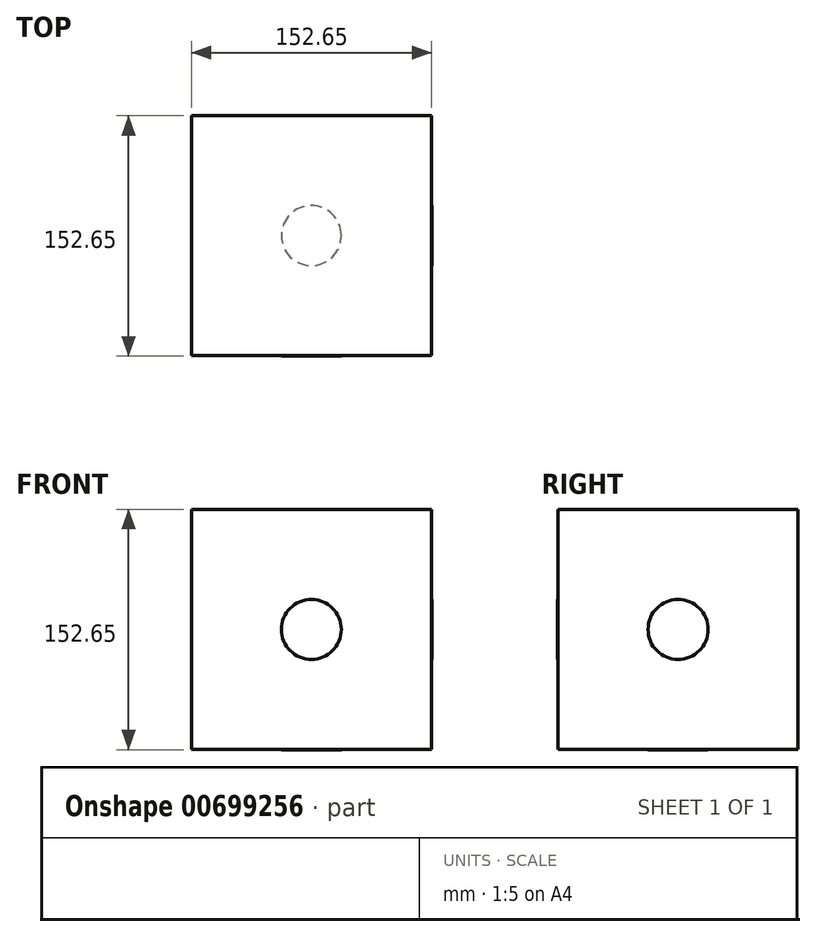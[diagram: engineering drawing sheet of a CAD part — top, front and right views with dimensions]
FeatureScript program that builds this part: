
annotation { "Feature Type Name" : "Feature", "Feature Type Description" : "" }
export const myFeature = defineFeature(function(context is Context, id is Id, definition is map)
    precondition{}
    {
        {
            var Q0;
            Q0=qCreatedBy(makeId("Top.planeOp"),FACE);
            var sketch = newSketch(context, id + "F0", { "sketchPlane" : qUnion([Q0])});
            skLineSegment(sketch, "E0.bottom", {"start": v(0, 0) * mm, "end": v(152.4, 0) * mm});
            skLineSegment(sketch, "E0.top", {"start": v(0, -152.4) * mm, "end": v(152.4, -152.4) * mm});
            skLineSegment(sketch, "E0.left", {"start": v(0, 0) * mm, "end": v(0, -152.4) * mm});
            skLineSegment(sketch, "E0.right", {"start": v(152.4, 0) * mm, "end": v(152.4, -152.4) * mm});
            skSolve(sketch);
        }
        {
            var Q0;
            Q0 = qSketchRegion(id + "F0", true);
            extrude(context, id + "F1", {"entities" : qUnion([Q0]), "depth" : 152.4 * mm, "offsetDistance" : 25.4 * mm});
        }
        {
            var Q0;
            Q0=makeQuery(id+"F1.opExtrude","SWEPT_FACE",FACE,{"disambiguationData":[OSD([sQuery(id+"F0.wireOp",EDGE,"E0.top")])]});
            var sketch = newSketch(context, id + "F2", { "sketchPlane" : qUnion([Q0])});
            skCircle(sketch, "E1", {"center": v(76.2, 76.2) * mm, "radius": 19.05 * mm});
            skPoint(sketch, "E1.centerSnap0", {"position": v(76.2, 0) * mm});
            skPoint(sketch, "E1.centerSnap1", {"position": v(0, 76.2) * mm});
            skSolve(sketch);
        }
        {
            var Q0;
            Q0=makeQuery(id+"F2.imprint","IMPRINT",FACE,{"disambiguationData":[TD([[makeQuery(id+"F2.imprint","IMPRINT",EDGE,{"derivedFrom":sQuery(id+"F2.wireOp",EDGE,"E1")}),1.0]])]});
            extrude(context, id + "F3", {"entities" : qUnion([Q0]), "operationType" : NewBodyOperationType.ADD, "depth" : 0.25 * mm, "offsetDistance" : 25.4 * mm});
        }
        {
            var Q0;
            Q0=makeQuery(id+"F1.opExtrude","SWEPT_FACE",FACE,{"disambiguationData":[OSD([sQuery(id+"F0.wireOp",EDGE,"E0.right")])]});
            var sketch = newSketch(context, id + "F4", { "sketchPlane" : qUnion([Q0])});
            skCircle(sketch, "E2", {"center": v(-76.2, 76.2) * mm, "radius": 19.05 * mm});
            skPoint(sketch, "E2.centerSnap0", {"position": v(-152.4, 76.2) * mm});
            skPoint(sketch, "E2.centerSnap1", {"position": v(-76.2, 0) * mm});
            skSolve(sketch);
        }
        {
            var Q0;
            Q0 = qSketchRegion(id + "F4", true);
            extrude(context, id + "F5", {"entities" : qUnion([Q0]), "operationType" : NewBodyOperationType.ADD, "depth" : 0.25 * mm, "offsetDistance" : 25.4 * mm});
        }
        {
            var Q0;
            Q0=makeQuery(id+"F1.opExtrude","CAP_FACE",FACE,{"disambiguationData":[OSD([sQuery(id+"F0.wireOp",EDGE,"E0.bottom"),sQuery(id+"F0.wireOp",EDGE,"E0.top"),sQuery(id+"F0.wireOp",EDGE,"E0.left"),sQuery(id+"F0.wireOp",EDGE,"E0.right")])],"isStart":true});
            var sketch = newSketch(context, id + "F6", { "sketchPlane" : qUnion([Q0])});
            skCircle(sketch, "E3", {"center": v(76.2, 76.2) * mm, "radius": 19.05 * mm});
            skPoint(sketch, "E3.centerSnap0", {"position": v(0, 76.2) * mm});
            skPoint(sketch, "E3.centerSnap1", {"position": v(76.2, 152.4) * mm});
            skSolve(sketch);
        }
        {
            var Q0;
            Q0 = qSketchRegion(id + "F6", true);
            extrude(context, id + "F7", {"entities" : qUnion([Q0]), "operationType" : NewBodyOperationType.ADD, "depth" : 0.25 * mm, "offsetDistance" : 25.4 * mm});
        }
    });
